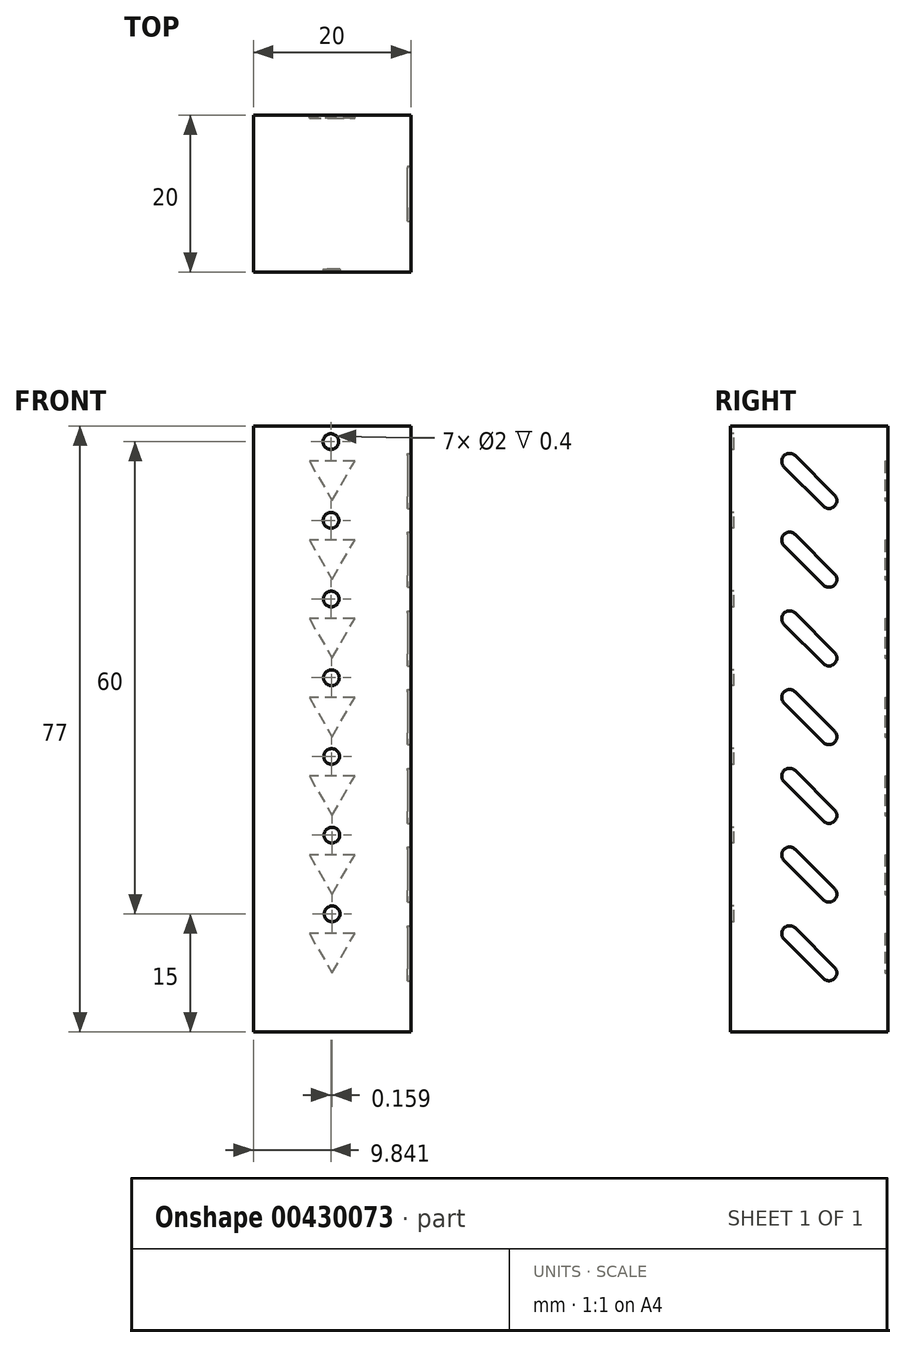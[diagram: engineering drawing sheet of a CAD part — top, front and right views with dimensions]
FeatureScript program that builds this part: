
annotation { "Feature Type Name" : "Feature", "Feature Type Description" : "" }
export const myFeature = defineFeature(function(context is Context, id is Id, definition is map)
    precondition{}
    {
        {
            var Q0;
            Q0=qCreatedBy(makeId("Top.planeOp"),FACE);
            var sketch = newSketch(context, id + "F0", { "sketchPlane" : qUnion([Q0])});
            skCircle(sketch, "E0", {"center": v(0, 0) * mm, "radius": 10 * mm});
            skLineSegment(sketch, "E1.bottom", {"start": v(10, 10) * mm, "end": v(-10, 10) * mm});
            skLineSegment(sketch, "E1.top", {"start": v(10, -10) * mm, "end": v(-10, -10) * mm});
            skLineSegment(sketch, "E1.left", {"start": v(10, 10) * mm, "end": v(10, -10) * mm});
            skLineSegment(sketch, "E1.right", {"start": v(-10, 10) * mm, "end": v(-10, -10) * mm});
            skSolve(sketch);
        }
        {
            var Q0;
            {var subQ0=sQuery(id+"F0.wireOp",EDGE,"E1.bottom");var subQ1=sQuery(id+"F0.wireOp",EDGE,"E0");var subQ2=makeQuery(id+"F0.imprint","INTERSECT",VERTEX,{"derivedFrom":[subQ1,subQ0]});Q0=makeQuery(id+"F0.imprint","IMPRINT",FACE,{"disambiguationData":[TD([[makeQuery(id+"F0.imprint","IMPRINT",EDGE,{"disambiguationData":[TD([[subQ2,-1.0]])],"derivedFrom":subQ1}),-1.0]])]});}
            var Q1;
            {var subQ0=sQuery(id+"F0.wireOp",EDGE,"E1.right");var subQ1=sQuery(id+"F0.wireOp",EDGE,"E0");var subQ2=makeQuery(id+"F0.imprint","INTERSECT",VERTEX,{"derivedFrom":[subQ1,subQ0]});Q1=makeQuery(id+"F0.imprint","IMPRINT",FACE,{"disambiguationData":[TD([[makeQuery(id+"F0.imprint","IMPRINT",EDGE,{"disambiguationData":[TD([[subQ2,-1.0]])],"derivedFrom":subQ1}),-1.0]])]});}
            var Q2;
            {var subQ0=sQuery(id+"F0.wireOp",EDGE,"E1.left");var subQ1=sQuery(id+"F0.wireOp",EDGE,"E0");var subQ2=makeQuery(id+"F0.imprint","INTERSECT",VERTEX,{"derivedFrom":[subQ1,subQ0]});Q2=makeQuery(id+"F0.imprint","IMPRINT",FACE,{"disambiguationData":[TD([[makeQuery(id+"F0.imprint","IMPRINT",EDGE,{"disambiguationData":[TD([[subQ2,1.0]])],"derivedFrom":subQ1}),-1.0]])]});}
            var Q3;
            {var subQ0=sQuery(id+"F0.wireOp",EDGE,"E1.bottom");var subQ1=sQuery(id+"F0.wireOp",EDGE,"E0");var subQ2=makeQuery(id+"F0.imprint","INTERSECT",VERTEX,{"derivedFrom":[subQ1,subQ0]});Q3=makeQuery(id+"F0.imprint","IMPRINT",FACE,{"disambiguationData":[TD([[makeQuery(id+"F0.imprint","IMPRINT",EDGE,{"disambiguationData":[TD([[subQ2,1.0]])],"derivedFrom":subQ1}),-1.0]])]});}
            var Q4;
            {var subQ0=sQuery(id+"F0.wireOp",EDGE,"E0");var subQ1=makeQuery(id+"F0.imprint","INTERSECT",VERTEX,{"derivedFrom":[subQ0,sQuery(id+"F0.wireOp",EDGE,"E1.bottom")]});Q4=makeQuery(id+"F0.imprint","IMPRINT",FACE,{"disambiguationData":[TD([[makeQuery(id+"F0.imprint","IMPRINT",EDGE,{"disambiguationData":[TD([[subQ1,1.0]])],"derivedFrom":subQ0}),1.0]])]});}
            extrude(context, id + "F1", {"entities" : qUnion([Q0, Q1, Q2, Q3, Q4]), "depth" : (7 * 10 + 7) * mm});
        }
        {
            var Q0;
            Q0=qCreatedBy(makeId("Front.planeOp"),FACE);
            cPlane(context, id + "F2", {"entities" : qUnion([Q0]), "cplaneType" : CPlaneType.OFFSET, "offset" : 10 * mm, "width" : 150 * mm, "height" : 150 * mm});
        }
        {
            var Q0;
            Q0=qCreatedBy(id+"F2.planeOp",FACE);
            var sketch = newSketch(context, id + "F3", { "sketchPlane" : qUnion([Q0])});
            skCircle(sketch, "E2", {"center": v(0, 15) * mm, "radius": 1 * mm});
            skCircle(sketch, "E3.1.0.0", {"center": v(-0.03, 25) * mm, "radius": 1 * mm});
            skCircle(sketch, "E3.2.0.0", {"center": v(-0.05, 35) * mm, "radius": 1 * mm});
            skCircle(sketch, "E3.3.0.0", {"center": v(-0.08, 45) * mm, "radius": 1 * mm});
            skCircle(sketch, "E3.4.0.0", {"center": v(-0.1, 55) * mm, "radius": 1 * mm});
            skCircle(sketch, "E3.5.0.0", {"center": v(-0.13, 65) * mm, "radius": 1 * mm});
            skCircle(sketch, "E3.6.0.0", {"center": v(-0.16, 75) * mm, "radius": 1 * mm});
            skLineSegment(sketch, "E3.direction1", {"start": v(0, 15) * mm, "end": v(-0.03, 25) * mm, "construction": true});
            skSolve(sketch);
        }
        {
            var Q0;
            Q0=qSketchRegion(id+"F3",true);
            extrude(context, id + "F4", {"entities" : qUnion([Q0]), "operationType" : NewBodyOperationType.REMOVE, "oppositeDirection" : true, "depth" : 0.4 * mm});
        }
        {
            var Q0;
            Q0=qCreatedBy(makeId("Right.planeOp"),FACE);
            cPlane(context, id + "F5", {"entities" : qUnion([Q0]), "cplaneType" : CPlaneType.OFFSET, "offset" : 10 * mm, "width" : 150 * mm, "height" : 150 * mm});
        }
        {
            var Q0;
            Q0=qCreatedBy(id+"F5.planeOp",FACE);
            var sketch = newSketch(context, id + "F6", { "sketchPlane" : qUnion([Q0])});
            skLineSegment(sketch, "E4", {"start": v(-2.5, 12.5) * mm, "end": v(2.5, 7.5) * mm, "construction": true});
            skLineSegment(sketch, "E5", {"start": v(2.5, 7.5) * mm, "end": v(0, 7.5) * mm, "construction": true});
            skPoint(sketch, "E5.endSnap0", {"position": v(0, 10) * mm});
            skArc(sketch, "E6.0.startCap", {"start": v(-3.2, 11.8) * mm, "mid": v(-3.2, 13.2) * mm, "end": v(-1.8, 13.2) * mm});
            skArc(sketch, "E6.0.endCap", {"start": v(3.2, 8.2) * mm, "mid": v(3.2, 6.8) * mm, "end": v(1.8, 6.8) * mm});
            skLineSegment(sketch, "E6.0.left", {"start": v(-1.8, 13.2) * mm, "end": v(3.2, 8.2) * mm});
            skLineSegment(sketch, "E6.0.right", {"start": v(-3.2, 11.8) * mm, "end": v(1.8, 6.8) * mm});
            skLineSegment(sketch, "E7.1.0.0", {"start": v(-2.5, 22.5) * mm, "end": v(2.5, 17.5) * mm, "construction": true});
            skArc(sketch, "E7.1.0.1", {"start": v(-3.2, 21.8) * mm, "mid": v(-3.2, 23.2) * mm, "end": v(-1.8, 23.2) * mm});
            skLineSegment(sketch, "E7.1.0.2", {"start": v(-3.2, 21.8) * mm, "end": v(1.8, 16.8) * mm});
            skLineSegment(sketch, "E7.1.0.3", {"start": v(-1.8, 23.2) * mm, "end": v(3.2, 18.2) * mm});
            skLineSegment(sketch, "E7.1.0.4", {"start": v(2.5, 17.5) * mm, "end": v(0, 17.5) * mm, "construction": true});
            skPoint(sketch, "E7.1.0.5", {"position": v(0, 20) * mm});
            skArc(sketch, "E7.1.0.6", {"start": v(3.2, 18.2) * mm, "mid": v(3.2, 16.8) * mm, "end": v(1.8, 16.8) * mm});
            skLineSegment(sketch, "E7.2.0.0", {"start": v(-2.5, 32.5) * mm, "end": v(2.5, 27.5) * mm, "construction": true});
            skArc(sketch, "E7.2.0.1", {"start": v(-3.2, 31.8) * mm, "mid": v(-3.2, 33.2) * mm, "end": v(-1.8, 33.2) * mm});
            skLineSegment(sketch, "E7.2.0.2", {"start": v(-3.2, 31.8) * mm, "end": v(1.8, 26.8) * mm});
            skLineSegment(sketch, "E7.2.0.3", {"start": v(-1.8, 33.2) * mm, "end": v(3.2, 28.2) * mm});
            skLineSegment(sketch, "E7.2.0.4", {"start": v(2.5, 27.5) * mm, "end": v(0, 27.5) * mm, "construction": true});
            skPoint(sketch, "E7.2.0.5", {"position": v(0, 30) * mm});
            skArc(sketch, "E7.2.0.6", {"start": v(3.2, 28.2) * mm, "mid": v(3.2, 26.8) * mm, "end": v(1.8, 26.8) * mm});
            skLineSegment(sketch, "E7.3.0.0", {"start": v(-2.5, 42.5) * mm, "end": v(2.5, 37.5) * mm, "construction": true});
            skArc(sketch, "E7.3.0.1", {"start": v(-3.2, 41.8) * mm, "mid": v(-3.2, 43.2) * mm, "end": v(-1.8, 43.2) * mm});
            skLineSegment(sketch, "E7.3.0.2", {"start": v(-3.2, 41.8) * mm, "end": v(1.8, 36.8) * mm});
            skLineSegment(sketch, "E7.3.0.3", {"start": v(-1.8, 43.2) * mm, "end": v(3.2, 38.2) * mm});
            skLineSegment(sketch, "E7.3.0.4", {"start": v(2.5, 37.5) * mm, "end": v(0, 37.5) * mm, "construction": true});
            skPoint(sketch, "E7.3.0.5", {"position": v(0, 40) * mm});
            skArc(sketch, "E7.3.0.6", {"start": v(3.2, 38.2) * mm, "mid": v(3.2, 36.8) * mm, "end": v(1.8, 36.8) * mm});
            skLineSegment(sketch, "E7.4.0.0", {"start": v(-2.5, 52.5) * mm, "end": v(2.5, 47.5) * mm, "construction": true});
            skArc(sketch, "E7.4.0.1", {"start": v(-3.2, 51.8) * mm, "mid": v(-3.2, 53.2) * mm, "end": v(-1.8, 53.2) * mm});
            skLineSegment(sketch, "E7.4.0.2", {"start": v(-3.2, 51.8) * mm, "end": v(1.8, 46.8) * mm});
            skLineSegment(sketch, "E7.4.0.3", {"start": v(-1.8, 53.2) * mm, "end": v(3.2, 48.2) * mm});
            skLineSegment(sketch, "E7.4.0.4", {"start": v(2.5, 47.5) * mm, "end": v(0, 47.5) * mm, "construction": true});
            skPoint(sketch, "E7.4.0.5", {"position": v(0, 50) * mm});
            skArc(sketch, "E7.4.0.6", {"start": v(3.2, 48.2) * mm, "mid": v(3.2, 46.8) * mm, "end": v(1.8, 46.8) * mm});
            skLineSegment(sketch, "E7.5.0.0", {"start": v(-2.5, 62.5) * mm, "end": v(2.5, 57.5) * mm, "construction": true});
            skArc(sketch, "E7.5.0.1", {"start": v(-3.2, 61.8) * mm, "mid": v(-3.2, 63.2) * mm, "end": v(-1.8, 63.2) * mm});
            skLineSegment(sketch, "E7.5.0.2", {"start": v(-3.2, 61.8) * mm, "end": v(1.8, 56.8) * mm});
            skLineSegment(sketch, "E7.5.0.3", {"start": v(-1.8, 63.2) * mm, "end": v(3.2, 58.2) * mm});
            skLineSegment(sketch, "E7.5.0.4", {"start": v(2.5, 57.5) * mm, "end": v(0, 57.5) * mm, "construction": true});
            skPoint(sketch, "E7.5.0.5", {"position": v(0, 60) * mm});
            skArc(sketch, "E7.5.0.6", {"start": v(3.2, 58.2) * mm, "mid": v(3.2, 56.8) * mm, "end": v(1.8, 56.8) * mm});
            skLineSegment(sketch, "E7.6.0.0", {"start": v(-2.5, 72.5) * mm, "end": v(2.5, 67.5) * mm, "construction": true});
            skArc(sketch, "E7.6.0.1", {"start": v(-3.2, 71.8) * mm, "mid": v(-3.2, 73.2) * mm, "end": v(-1.8, 73.2) * mm});
            skLineSegment(sketch, "E7.6.0.2", {"start": v(-3.2, 71.8) * mm, "end": v(1.8, 66.8) * mm});
            skLineSegment(sketch, "E7.6.0.3", {"start": v(-1.8, 73.2) * mm, "end": v(3.2, 68.2) * mm});
            skLineSegment(sketch, "E7.6.0.4", {"start": v(2.5, 67.5) * mm, "end": v(0, 67.5) * mm, "construction": true});
            skPoint(sketch, "E7.6.0.5", {"position": v(0, 70) * mm});
            skArc(sketch, "E7.6.0.6", {"start": v(3.2, 68.2) * mm, "mid": v(3.2, 66.8) * mm, "end": v(1.8, 66.8) * mm});
            skLineSegment(sketch, "E7.direction1", {"start": v(0, 7.5) * mm, "end": v(0, 17.5) * mm, "construction": true});
            skSolve(sketch);
        }
        {
            var Q0;
            Q0=qSketchRegion(id+"F6",true);
            var Q1;
            Q1=makeQuery(id+"F1.opExtrude","SWEPT_FACE",FACE,{"disambiguationData":[OSD([sQuery(id+"F0.wireOp",EDGE,"E1.right")])]});
            extrude(context, id + "F7", {"entities" : qUnion([Q0, Q1]), "operationType" : NewBodyOperationType.REMOVE, "oppositeDirection" : true, "depth" : 0.4 * mm});
        }
        {
            var Q0;
            Q0=qCreatedBy(makeId("Front.planeOp"),FACE);
            cPlane(context, id + "F8", {"entities" : qUnion([Q0]), "cplaneType" : CPlaneType.OFFSET, "offset" : 10 * mm, "oppositeDirection" : true, "width" : 150 * mm, "height" : 150 * mm});
        }
        {
            var Q0;
            Q0=qCreatedBy(id+"F8.planeOp",FACE);
            var sketch = newSketch(context, id + "F9", { "sketchPlane" : qUnion([Q0])});
            skLineSegment(sketch, "E8", {"start": v(-2.89, 12.5) * mm, "end": v(0, 7.5) * mm});
            skLineSegment(sketch, "E9", {"start": v(0, 7.5) * mm, "end": v(2.89, 12.5) * mm});
            skLineSegment(sketch, "E10", {"start": v(2.89, 12.5) * mm, "end": v(-2.89, 12.5) * mm});
            skLineSegment(sketch, "E11.1.0.0", {"start": v(0, 17.5) * mm, "end": v(2.89, 22.5) * mm});
            skLineSegment(sketch, "E11.1.0.1", {"start": v(2.89, 22.5) * mm, "end": v(-2.89, 22.5) * mm});
            skLineSegment(sketch, "E11.1.0.2", {"start": v(-2.89, 22.5) * mm, "end": v(0, 17.5) * mm});
            skLineSegment(sketch, "E11.2.0.0", {"start": v(0, 27.5) * mm, "end": v(2.89, 32.5) * mm});
            skLineSegment(sketch, "E11.2.0.1", {"start": v(2.89, 32.5) * mm, "end": v(-2.89, 32.5) * mm});
            skLineSegment(sketch, "E11.2.0.2", {"start": v(-2.89, 32.5) * mm, "end": v(0, 27.5) * mm});
            skLineSegment(sketch, "E11.3.0.0", {"start": v(0, 37.5) * mm, "end": v(2.89, 42.5) * mm});
            skLineSegment(sketch, "E11.3.0.1", {"start": v(2.89, 42.5) * mm, "end": v(-2.89, 42.5) * mm});
            skLineSegment(sketch, "E11.3.0.2", {"start": v(-2.89, 42.5) * mm, "end": v(0, 37.5) * mm});
            skLineSegment(sketch, "E11.4.0.0", {"start": v(0, 47.5) * mm, "end": v(2.89, 52.5) * mm});
            skLineSegment(sketch, "E11.4.0.1", {"start": v(2.89, 52.5) * mm, "end": v(-2.89, 52.5) * mm});
            skLineSegment(sketch, "E11.4.0.2", {"start": v(-2.89, 52.5) * mm, "end": v(0, 47.5) * mm});
            skLineSegment(sketch, "E11.5.0.0", {"start": v(0, 57.5) * mm, "end": v(2.89, 62.5) * mm});
            skLineSegment(sketch, "E11.5.0.1", {"start": v(2.89, 62.5) * mm, "end": v(-2.89, 62.5) * mm});
            skLineSegment(sketch, "E11.5.0.2", {"start": v(-2.89, 62.5) * mm, "end": v(0, 57.5) * mm});
            skLineSegment(sketch, "E11.6.0.0", {"start": v(0, 67.5) * mm, "end": v(2.89, 72.5) * mm});
            skLineSegment(sketch, "E11.6.0.1", {"start": v(2.89, 72.5) * mm, "end": v(-2.89, 72.5) * mm});
            skLineSegment(sketch, "E11.6.0.2", {"start": v(-2.89, 72.5) * mm, "end": v(0, 67.5) * mm});
            skLineSegment(sketch, "E11.direction1", {"start": v(0, 7.5) * mm, "end": v(0, 17.5) * mm, "construction": true});
            skSolve(sketch);
        }
        {
            var Q0;
            Q0=qSketchRegion(id+"F9",true);
            extrude(context, id + "F10", {"entities" : qUnion([Q0]), "operationType" : NewBodyOperationType.REMOVE, "depth" : 0.4 * mm});
        }
    });
